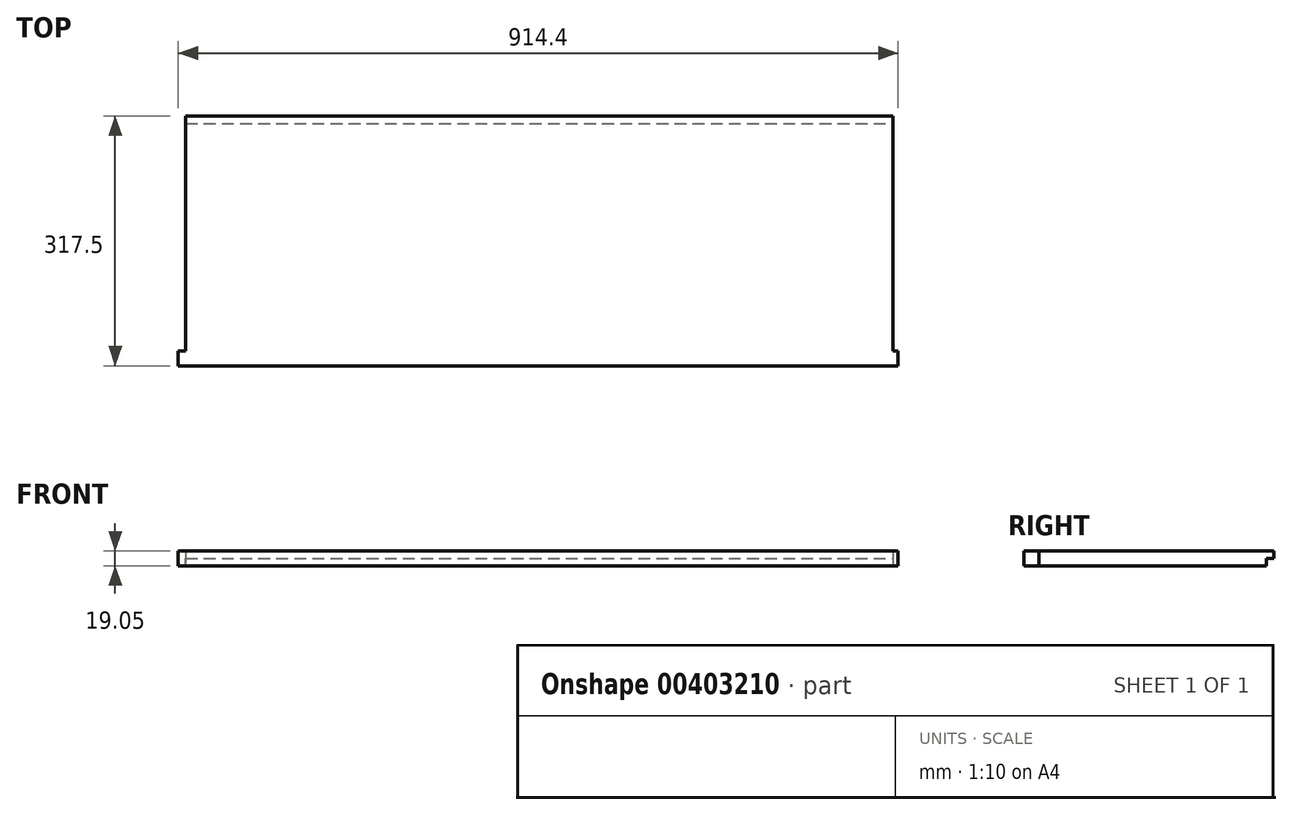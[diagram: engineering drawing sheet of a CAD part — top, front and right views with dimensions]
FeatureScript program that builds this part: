
annotation { "Feature Type Name" : "Feature", "Feature Type Description" : "" }
export const myFeature = defineFeature(function(context is Context, id is Id, definition is map)
    precondition{}
    {
        {
            var Q0;
            Q0=qCreatedBy(makeId("Top.planeOp"),FACE);
            var sketch = newSketch(context, id + "F0", { "sketchPlane" : qUnion([Q0])});
            skLineSegment(sketch, "E0.bottom", {"start": v(449.26, -158.75) * mm, "end": v(-449.26, -158.75) * mm});
            skLineSegment(sketch, "E0.top", {"start": v(449.26, 158.75) * mm, "end": v(-449.26, 158.75) * mm});
            skLineSegment(sketch, "E0.left", {"start": v(449.26, -158.75) * mm, "end": v(449.26, 158.75) * mm});
            skLineSegment(sketch, "E0.right", {"start": v(-449.26, -158.75) * mm, "end": v(-449.26, 158.75) * mm});
            skPoint(sketch, "E0.middle", {"position": v(0, 0) * mm});
            skSolve(sketch);
        }
        {
            var Q0;
            Q0=qSketchRegion(id+"F0",true);
            extrude(context, id + "F1", {"entities" : qUnion([Q0]), "depth" : 19.05 * mm});
        }
        {
            var Q0;
            Q0=makeQuery(id+"F1.opExtrude","SWEPT_FACE",FACE,{"disambiguationData":[OSD([sQuery(id+"F0.wireOp",EDGE,"E0.left")])]});
            var sketch = newSketch(context, id + "F2", { "sketchPlane" : qUnion([Q0])});
            skLineSegment(sketch, "E1.bottom", {"start": v(149.22, 9.53) * mm, "end": v(158.75, 9.53) * mm});
            skLineSegment(sketch, "E1.top", {"start": v(149.22, 0) * mm, "end": v(158.75, 0) * mm});
            skLineSegment(sketch, "E1.left", {"start": v(149.22, 9.53) * mm, "end": v(149.22, 0) * mm});
            skLineSegment(sketch, "E1.right", {"start": v(158.75, 9.52) * mm, "end": v(158.75, 0) * mm});
            skSolve(sketch);
        }
        {
            var Q0;
            Q0=qSketchRegion(id+"F2",true);
            extrude(context, id + "F3", {"entities" : qUnion([Q0]), "operationType" : NewBodyOperationType.REMOVE, "endBound" : BoundingType.THROUGH_ALL, "oppositeDirection" : true, "depth" : 25.4 * mm});
        }
        {
            var Q0;
            Q0=makeQuery(id+"F1.opExtrude","SWEPT_FACE",FACE,{"disambiguationData":[OSD([sQuery(id+"F0.wireOp",EDGE,"E0.right")])]});
            var sketch = newSketch(context, id + "F4", { "sketchPlane" : qUnion([Q0])});
            skLineSegment(sketch, "E2.bottom", {"start": v(158.75, 19.05) * mm, "end": v(139.7, 19.05) * mm});
            skLineSegment(sketch, "E2.top", {"start": v(158.75, 0) * mm, "end": v(139.7, 0) * mm});
            skLineSegment(sketch, "E2.left", {"start": v(158.75, 19.05) * mm, "end": v(158.75, 0) * mm});
            skLineSegment(sketch, "E2.right", {"start": v(139.7, 19.05) * mm, "end": v(139.7, 0) * mm});
            skSolve(sketch);
        }
        {
            var Q0;
            Q0=qSketchRegion(id+"F4",true);
            extrude(context, id + "F5", {"entities" : qUnion([Q0]), "operationType" : NewBodyOperationType.ADD, "depth" : 9.52 * mm});
        }
        {
            var Q0;
            Q0=makeQuery(id+"F1.opExtrude","SWEPT_FACE",FACE,{"disambiguationData":[OSD([sQuery(id+"F0.wireOp",EDGE,"E0.left")])]});
            var sketch = newSketch(context, id + "F6", { "sketchPlane" : qUnion([Q0])});
            skLineSegment(sketch, "E3.0.0", {"start": v(-158.75, 19.05) * mm, "end": v(-139.7, 19.05) * mm});
            skLineSegment(sketch, "E3.0.1", {"start": v(-139.7, 19.05) * mm, "end": v(-139.7, 0) * mm});
            skLineSegment(sketch, "E3.0.2", {"start": v(-139.7, 0) * mm, "end": v(-158.75, 0) * mm});
            skLineSegment(sketch, "E3.0.3", {"start": v(-158.75, 0) * mm, "end": v(-158.75, 19.05) * mm});
            skSolve(sketch);
        }
        {
            var Q0;
            Q0=qSketchRegion(id+"F6",true);
            extrude(context, id + "F7", {"entities" : qUnion([Q0]), "operationType" : NewBodyOperationType.ADD, "depth" : 6.35 * mm});
        }
    });
